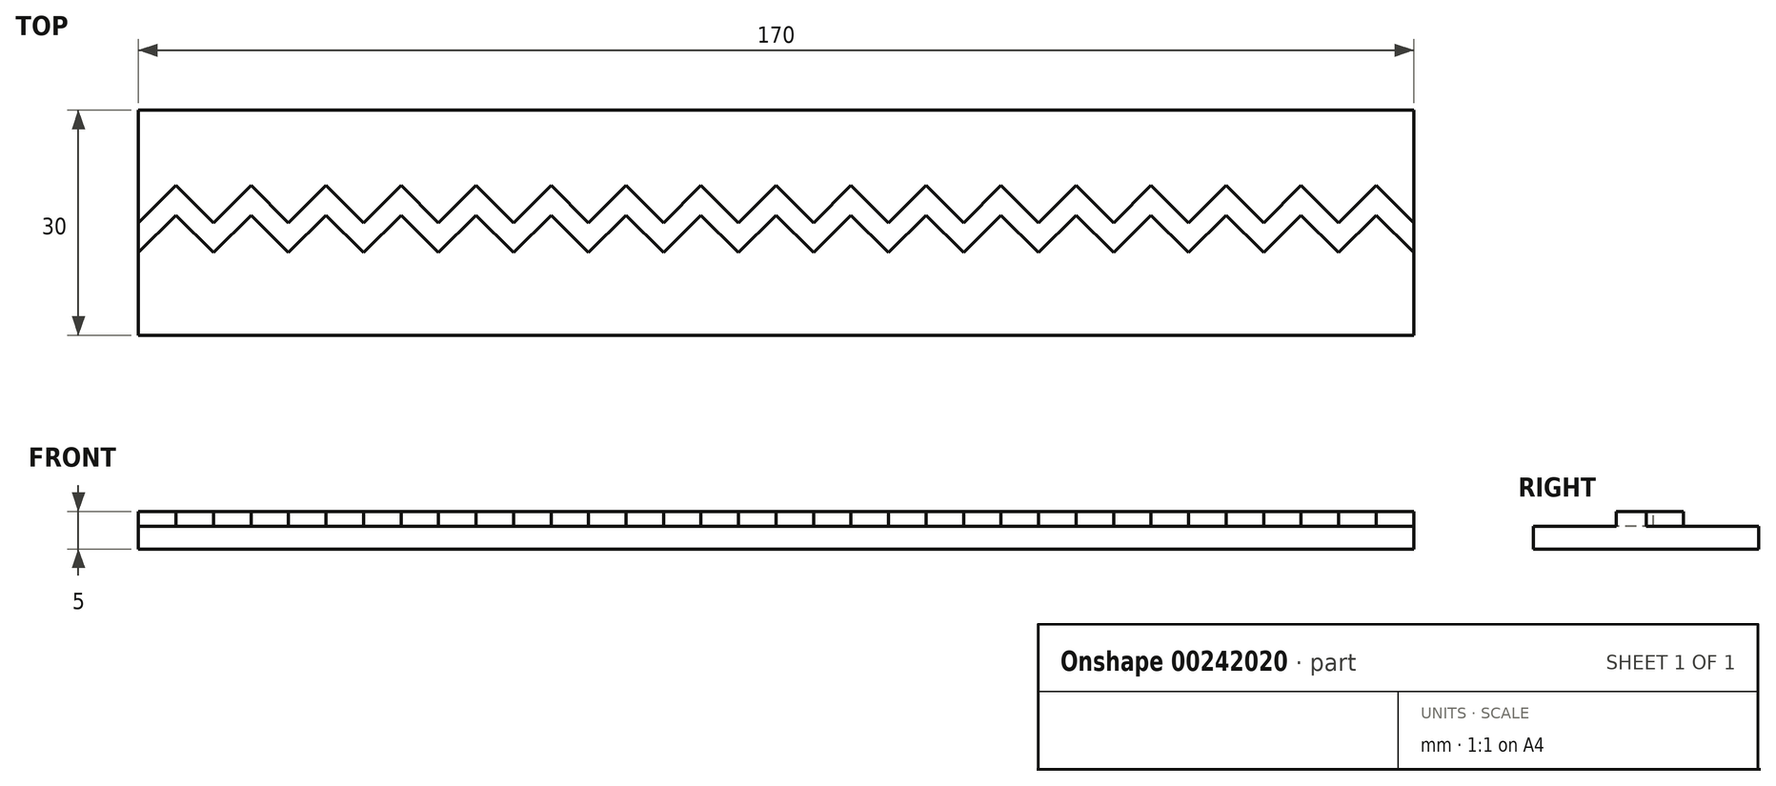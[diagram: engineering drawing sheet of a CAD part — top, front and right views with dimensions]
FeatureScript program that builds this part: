
annotation { "Feature Type Name" : "Feature", "Feature Type Description" : "" }
export const myFeature = defineFeature(function(context is Context, id is Id, definition is map)
    precondition{}
    {
        {
            var Q0;
            Q0=qCreatedBy(makeId("Top.planeOp"),FACE);
            var sketch = newSketch(context, id + "F0", { "sketchPlane" : qUnion([Q0])});
            skLineSegment(sketch, "E0.bottom", {"start": v(0, 30) * mm, "end": v(170, 30) * mm});
            skLineSegment(sketch, "E0.top", {"start": v(0, 0) * mm, "end": v(170, 0) * mm});
            skLineSegment(sketch, "E0.left", {"start": v(0, 30) * mm, "end": v(0, 0) * mm});
            skLineSegment(sketch, "E0.right", {"start": v(170, 30) * mm, "end": v(170, 0) * mm});
            skSolve(sketch);
        }
        {
            var Q0;
            Q0=makeQuery(id+"F0.imprint","IMPRINT",FACE,{"disambiguationData":[TD([[makeQuery(id+"F0.imprint","IMPRINT",EDGE,{"derivedFrom":sQuery(id+"F0.wireOp",EDGE,"E0.bottom")}),-1.0]])]});
            extrude(context, id + "F1", {"entities" : qUnion([Q0]), "depth" : 3 * mm});
        }
        {
            var Q0;
            Q0=makeQuery(id+"F1.opExtrude","CAP_FACE",FACE,{"disambiguationData":[OSD([sQuery(id+"F0.wireOp",EDGE,"E0.bottom"),sQuery(id+"F0.wireOp",EDGE,"E0.top"),sQuery(id+"F0.wireOp",EDGE,"E0.left"),sQuery(id+"F0.wireOp",EDGE,"E0.right")])],"isStart":false});
            var sketch = newSketch(context, id + "F2", { "sketchPlane" : qUnion([Q0])});
            skLineSegment(sketch, "E1", {"start": v(0, 15) * mm, "end": v(170, 15) * mm, "construction": true});
            skLineSegment(sketch, "E2", {"start": v(0, 15) * mm, "end": v(5, 20) * mm});
            skLineSegment(sketch, "E3", {"start": v(5, 20) * mm, "end": v(10, 15) * mm});
            skLineSegment(sketch, "E4.1.0.0", {"start": v(10, 15) * mm, "end": v(15, 20) * mm});
            skLineSegment(sketch, "E4.1.0.1", {"start": v(15, 20) * mm, "end": v(20, 15) * mm});
            skLineSegment(sketch, "E4.2.0.0", {"start": v(20, 15) * mm, "end": v(25, 20) * mm});
            skLineSegment(sketch, "E4.2.0.1", {"start": v(25, 20) * mm, "end": v(30, 15) * mm});
            skLineSegment(sketch, "E4.direction1", {"start": v(0, 15) * mm, "end": v(10, 15) * mm, "construction": true});
            skLineSegment(sketch, "E5.0.3.0", {"start": v(30, 15) * mm, "end": v(35, 20) * mm});
            skLineSegment(sketch, "E5.3.3.0", {"start": v(35, 20) * mm, "end": v(40, 15) * mm});
            skLineSegment(sketch, "E5.0.4.0", {"start": v(40, 15) * mm, "end": v(45, 20) * mm});
            skLineSegment(sketch, "E5.3.4.0", {"start": v(45, 20) * mm, "end": v(50, 15) * mm});
            skLineSegment(sketch, "E5.0.5.0", {"start": v(50, 15) * mm, "end": v(55, 20) * mm});
            skLineSegment(sketch, "E5.3.5.0", {"start": v(55, 20) * mm, "end": v(60, 15) * mm});
            skLineSegment(sketch, "E5.0.6.0", {"start": v(60, 15) * mm, "end": v(65, 20) * mm});
            skLineSegment(sketch, "E5.3.6.0", {"start": v(65, 20) * mm, "end": v(70, 15) * mm});
            skLineSegment(sketch, "E5.0.7.0", {"start": v(70, 15) * mm, "end": v(75, 20) * mm});
            skLineSegment(sketch, "E5.3.7.0", {"start": v(75, 20) * mm, "end": v(80, 15) * mm});
            skLineSegment(sketch, "E5.0.8.0", {"start": v(80, 15) * mm, "end": v(85, 20) * mm});
            skLineSegment(sketch, "E5.3.8.0", {"start": v(85, 20) * mm, "end": v(90, 15) * mm});
            skLineSegment(sketch, "E5.0.9.0", {"start": v(90, 15) * mm, "end": v(95, 20) * mm});
            skLineSegment(sketch, "E5.3.9.0", {"start": v(95, 20) * mm, "end": v(100, 15) * mm});
            skLineSegment(sketch, "E5.0.10.0", {"start": v(100, 15) * mm, "end": v(105, 20) * mm});
            skLineSegment(sketch, "E5.3.10.0", {"start": v(105, 20) * mm, "end": v(110, 15) * mm});
            skLineSegment(sketch, "E5.0.11.0", {"start": v(110, 15) * mm, "end": v(115, 20) * mm});
            skLineSegment(sketch, "E5.3.11.0", {"start": v(115, 20) * mm, "end": v(120, 15) * mm});
            skLineSegment(sketch, "E5.0.12.0", {"start": v(120, 15) * mm, "end": v(125, 20) * mm});
            skLineSegment(sketch, "E5.3.12.0", {"start": v(125, 20) * mm, "end": v(130, 15) * mm});
            skLineSegment(sketch, "E5.0.13.0", {"start": v(130, 15) * mm, "end": v(135, 20) * mm});
            skLineSegment(sketch, "E5.3.13.0", {"start": v(135, 20) * mm, "end": v(140, 15) * mm});
            skLineSegment(sketch, "E5.0.14.0", {"start": v(140, 15) * mm, "end": v(145, 20) * mm});
            skLineSegment(sketch, "E5.3.14.0", {"start": v(145, 20) * mm, "end": v(150, 15) * mm});
            skLineSegment(sketch, "E5.0.15.0", {"start": v(150, 15) * mm, "end": v(155, 20) * mm});
            skLineSegment(sketch, "E5.3.15.0", {"start": v(155, 20) * mm, "end": v(160, 15) * mm});
            skLineSegment(sketch, "E5.0.16.0", {"start": v(160, 15) * mm, "end": v(165, 20) * mm});
            skLineSegment(sketch, "E5.3.16.0", {"start": v(165, 20) * mm, "end": v(170, 15) * mm});
            skSolve(sketch);
        }
        {
            var Q0;
            Q0=makeQuery(id+"F1.opExtrude","SWEPT_FACE",FACE,{"disambiguationData":[OSD([sQuery(id+"F0.wireOp",EDGE,"E0.left")])]});
            var sketch = newSketch(context, id + "F3", { "sketchPlane" : qUnion([Q0])});
            skLineSegment(sketch, "E6.bottom", {"start": v(-15, 3) * mm, "end": v(-11, 3) * mm});
            skLineSegment(sketch, "E6.top", {"start": v(-15, 5) * mm, "end": v(-11, 5) * mm});
            skLineSegment(sketch, "E6.left", {"start": v(-15, 3) * mm, "end": v(-15, 5) * mm});
            skLineSegment(sketch, "E6.right", {"start": v(-11, 3) * mm, "end": v(-11, 5) * mm});
            skLineSegment(sketch, "E7.bottom", {"start": v(-13.75, 5) * mm, "end": v(-12.25, 5) * mm});
            skLineSegment(sketch, "E7.top", {"start": v(-13.75, 18) * mm, "end": v(-12.25, 18) * mm});
            skLineSegment(sketch, "E7.left", {"start": v(-13.75, 5) * mm, "end": v(-13.75, 18) * mm});
            skLineSegment(sketch, "E7.right", {"start": v(-12.25, 5) * mm, "end": v(-12.25, 18) * mm});
            skSolve(sketch);
        }
        {
            var Q0;
            Q0=makeQuery(id+"F3.imprint","IMPRINT",FACE,{"disambiguationData":[TD([[makeQuery(id+"F3.imprint","IMPRINT",EDGE,{"derivedFrom":sQuery(id+"F3.wireOp",EDGE,"E7.bottom")}),1.0]])]});
            var Q1;
            Q1=makeQuery(id+"F3.imprint","IMPRINT",FACE,{"disambiguationData":[TD([[makeQuery(id+"F3.imprint","IMPRINT",EDGE,{"derivedFrom":sQuery(id+"F3.wireOp",EDGE,"E6.bottom")}),1.0]])]});
            var Q2;
            Q2 = qConstructionFilter(qBodyType(qCreatedBy(id + "F2" ,EDGE), BodyType.WIRE), ConstructionObject.NO);
            sweep(context, id + "F4", {"operationType" : NewBodyOperationType.ADD, "profiles" : qUnion([Q0, Q1]), "path" : qUnion([Q2]), "keepProfileOrientation" : true});
        }
    });
